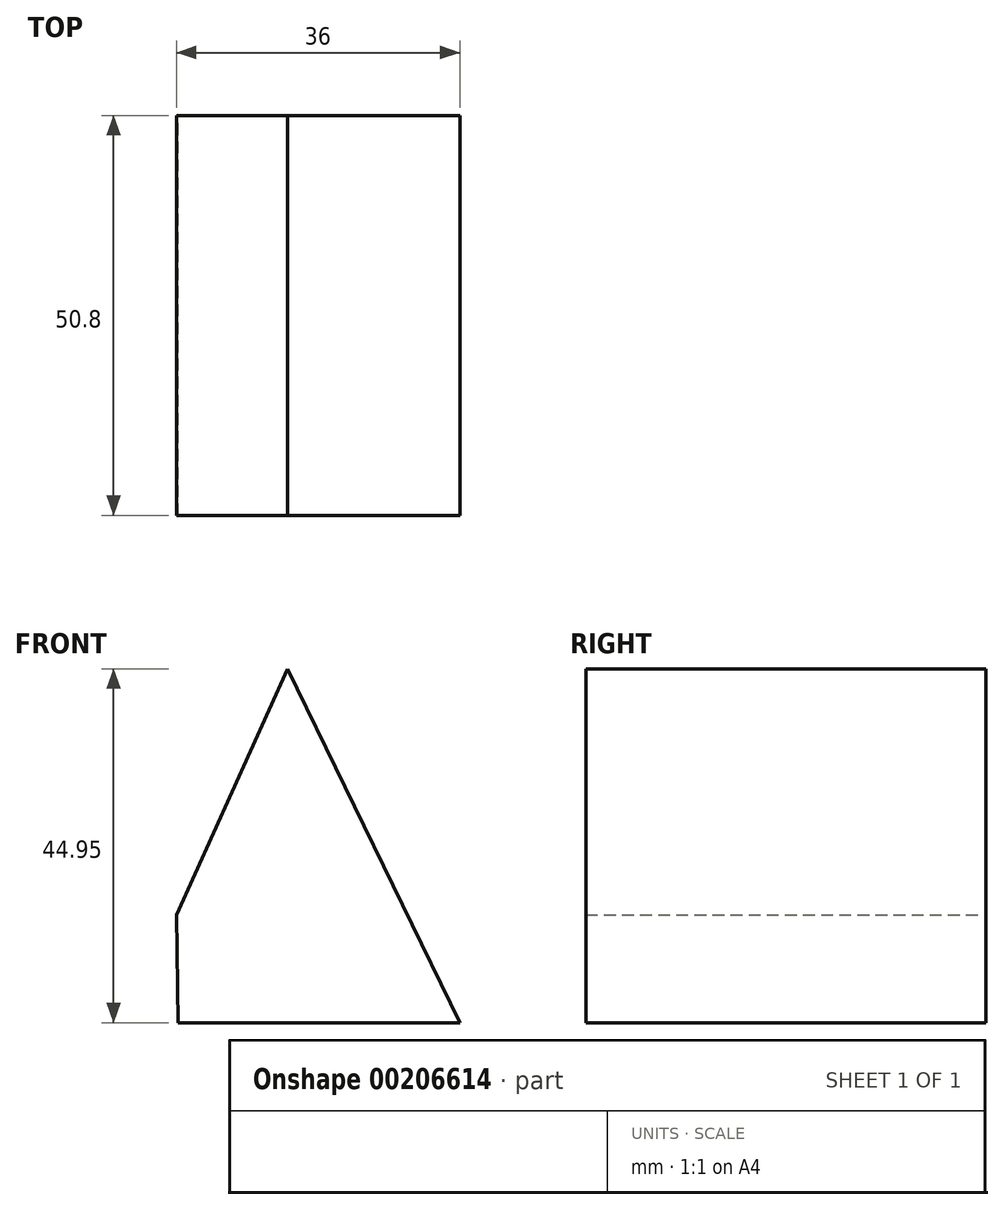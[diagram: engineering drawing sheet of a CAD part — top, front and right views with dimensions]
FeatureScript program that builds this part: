
annotation { "Feature Type Name" : "Feature", "Feature Type Description" : "" }
export const myFeature = defineFeature(function(context is Context, id is Id, definition is map)
    precondition{}
    {
        {
            var Q0;
            Q0=qCreatedBy(makeId("Front.planeOp"),FACE);
            var sketch = newSketch(context, id + "F0", { "sketchPlane" : qUnion([Q0])});
            skLineSegment(sketch, "E0", {"start": v(-36, 13.66) * mm, "end": v(-21.86, 44.95) * mm});
            skLineSegment(sketch, "E1", {"start": v(-21.86, 44.95) * mm, "end": v(0, 0) * mm});
            skLineSegment(sketch, "E2", {"start": v(0, 0) * mm, "end": v(-35.81, 0) * mm});
            skLineSegment(sketch, "E3", {"start": v(-35.81, 0) * mm, "end": v(-36, 13.66) * mm});
            skSolve(sketch);
        }
        {
            var Q0;
            Q0 = qSketchRegion(id + "F0", true);
            extrude(context, id + "F1", {"entities" : qUnion([Q0]), "depth" : 50.8 * mm});
        }
    });
